# Revit family: Thorn OMEGA C
name_source: partatom
category: Lighting Fixtures
revit_build: Autodesk Revit 2016 (Build: 20150220_1215(x64)
units: mm (PartAtom-declared; Revit-internal decimal feet)

## family parameters
Cut with Voids When Loaded = No
Host = Face
Light Source = Yes
OmniClass Number = 23.80.70.11
OmniClass Title = Luminaries for Internal Lighting
Part Type = Normal
Room Calculation Point = No
Round Connector Dimension = Use Diameter
Shared = No

## types (3) — shared parameters
Assembly Code = D5020200
Body = Thorn_Metal_White
Color Filter = 16777215
Cover = Thorn_PMMA
Description = LED luminaire
Dimming Lamp Color Temperature Shift = <None>
Emit Shape Visible in Rendering = No
Height = 55 mm  [stored 0.180446 ft]
Lamp = LED
Manufacturer = Thorn Lighting
Tilt Angle = -90.00°
Voltage = 230 V
zero-valued in all types: Default Elevation

## per-type parameters (varying)
| type | Apparent Load | Emit from Circle Diameter | Length | Model | Photometric Web File | URL | Width |
| OMEGA C LED1500 R300 | 33 VA | 380 mm | 400 mm | 96627771 | TLTP_OMGC_400R.IES | www.thornlighting.com/96627771 | 400 mm |
| OMEGA C LED2800 R400 | 33 VA | 380 mm | 400 mm | 96627771 | TLTP_OMGC_400R.IES | www.thornlighting.com/96627771 | 400 mm |
| OMEGA C LED3200 R500 | 42 VA | 480 mm | 500 mm  [stored 1.64042 ft] | 96627779 | TLTP_OMGC_500R.IES | www.thornlighting.com/96627779 | 500 mm  [stored 1.64042 ft] |

note: [stored X ft] marks values corroborated as IEEE doubles in the binary element streams (Revit-internal decimal feet)

## geometry (parser evidence)
native form markers: Sweep x3
no freeform markers — native parametric forms only
